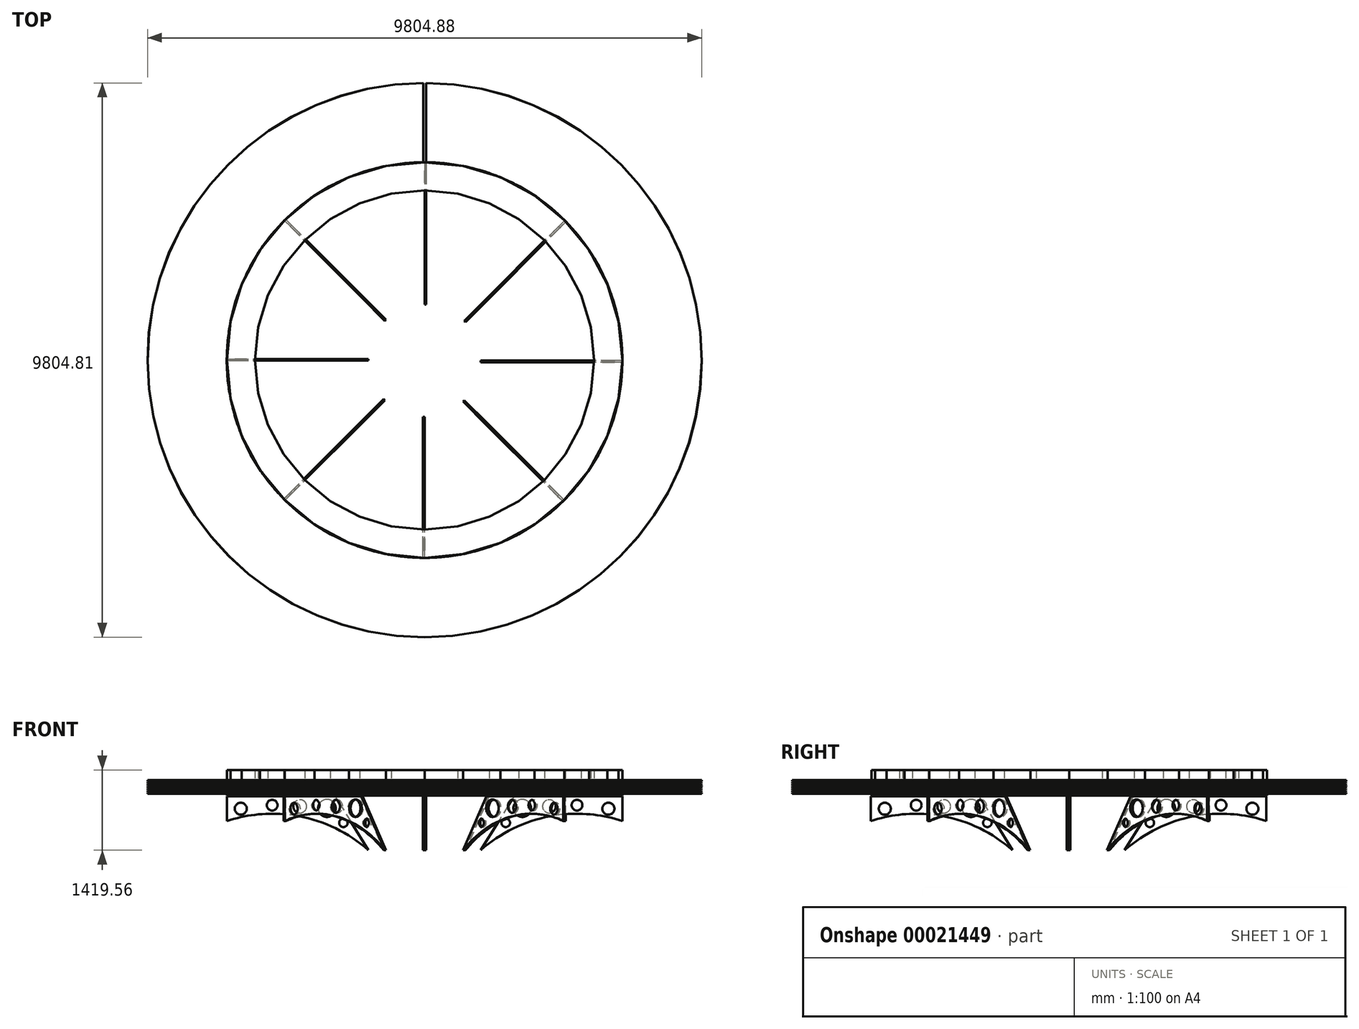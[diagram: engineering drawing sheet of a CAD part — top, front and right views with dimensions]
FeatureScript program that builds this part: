
annotation { "Feature Type Name" : "Feature", "Feature Type Description" : "" }
export const myFeature = defineFeature(function(context is Context, id is Id, definition is map)
    precondition{}
    {
        {
            var Q0;
            Q0=qCreatedBy(makeId("Right.planeOp"),FACE);
            var sketch = newSketch(context, id + "F0", { "sketchPlane" : qUnion([Q0])});
            skLineSegment(sketch, "E0", {"start": v(0, -239.01) * mm, "end": v(0, 243.44) * mm, "construction": true});
            skLineSegment(sketch, "E1", {"start": v(3500, 46.8) * mm, "end": v(3500, -314.16) * mm, "construction": true});
            skLineSegment(sketch, "E2.bottom", {"start": v(3502.44, -51) * mm, "end": v(4902.44, -51) * mm});
            skLineSegment(sketch, "E2.top", {"start": v(3502.44, -70.04) * mm, "end": v(4902.44, -70.04) * mm});
            skLineSegment(sketch, "E2.left", {"start": v(3502.44, -51) * mm, "end": v(3502.44, -70.04) * mm});
            skLineSegment(sketch, "E2.right", {"start": v(4902.44, -51) * mm, "end": v(4902.44, -70.04) * mm});
            skLineSegment(sketch, "E3.bottom", {"start": v(3501.2, 44.95) * mm, "end": v(4901.2, 44.95) * mm});
            skLineSegment(sketch, "E3.top", {"start": v(3501.2, 25.9) * mm, "end": v(4901.2, 25.9) * mm});
            skLineSegment(sketch, "E3.left", {"start": v(3501.2, 44.95) * mm, "end": v(3501.2, 25.9) * mm});
            skLineSegment(sketch, "E3.right", {"start": v(4901.2, 44.95) * mm, "end": v(4901.2, 25.9) * mm});
            skLineSegment(sketch, "E4.bottom", {"start": v(3500.35, 11.59) * mm, "end": v(4900.35, 11.59) * mm});
            skLineSegment(sketch, "E4.top", {"start": v(3500.35, -7.46) * mm, "end": v(4900.35, -7.46) * mm});
            skLineSegment(sketch, "E4.left", {"start": v(3500.35, 11.59) * mm, "end": v(3500.35, -7.46) * mm});
            skLineSegment(sketch, "E4.right", {"start": v(4900.35, 11.59) * mm, "end": v(4900.35, -7.46) * mm});
            skLineSegment(sketch, "E5.bottom", {"start": v(3500.35, -19.24) * mm, "end": v(4900.35, -19.24) * mm});
            skLineSegment(sketch, "E5.top", {"start": v(3500.35, -38.3) * mm, "end": v(4900.35, -38.3) * mm});
            skLineSegment(sketch, "E5.left", {"start": v(3500.35, -19.24) * mm, "end": v(3500.35, -38.3) * mm});
            skLineSegment(sketch, "E5.right", {"start": v(4900.35, -19.24) * mm, "end": v(4900.35, -38.3) * mm});
            skLineSegment(sketch, "E6.bottom", {"start": v(3500.35, -82.57) * mm, "end": v(4900.35, -82.57) * mm});
            skLineSegment(sketch, "E6.top", {"start": v(3500.35, -101.62) * mm, "end": v(4900.35, -101.62) * mm});
            skLineSegment(sketch, "E6.left", {"start": v(3500.35, -82.57) * mm, "end": v(3500.35, -101.62) * mm});
            skLineSegment(sketch, "E6.right", {"start": v(4900.35, -82.57) * mm, "end": v(4900.35, -101.62) * mm});
            skLineSegment(sketch, "E7.bottom", {"start": v(3500.32, -114.32) * mm, "end": v(4900.32, -114.32) * mm});
            skLineSegment(sketch, "E7.top", {"start": v(3500.32, -133.37) * mm, "end": v(4900.32, -133.37) * mm});
            skLineSegment(sketch, "E7.left", {"start": v(3500.32, -114.32) * mm, "end": v(3500.32, -133.37) * mm});
            skLineSegment(sketch, "E7.right", {"start": v(4900.32, -114.32) * mm, "end": v(4900.32, -133.37) * mm});
            skLineSegment(sketch, "E8.bottom", {"start": v(3499.61, -146.07) * mm, "end": v(4899.61, -146.07) * mm});
            skLineSegment(sketch, "E8.top", {"start": v(3499.61, -165.12) * mm, "end": v(4899.61, -165.12) * mm});
            skLineSegment(sketch, "E8.left", {"start": v(3499.61, -146.07) * mm, "end": v(3499.61, -165.12) * mm});
            skLineSegment(sketch, "E8.right", {"start": v(4899.61, -146.07) * mm, "end": v(4899.61, -165.12) * mm});
            skLineSegment(sketch, "E9.bottom", {"start": v(3501.02, -177.82) * mm, "end": v(4901.02, -177.82) * mm});
            skLineSegment(sketch, "E9.top", {"start": v(3501.02, -196.87) * mm, "end": v(4901.02, -196.87) * mm});
            skLineSegment(sketch, "E9.left", {"start": v(3501.02, -177.82) * mm, "end": v(3501.02, -196.87) * mm});
            skLineSegment(sketch, "E9.right", {"start": v(4901.02, -177.82) * mm, "end": v(4901.02, -196.87) * mm});
            skSolve(sketch);
        }
        {
            var Q0;
            Q0 = qSketchRegion(id + "F0", true);
            var Q1;
            Q1=makeQuery(id+"F0.imprint","IMPRINT",FACE,{"disambiguationData":[TD([[makeQuery(id+"F0.imprint","IMPRINT",EDGE,{"derivedFrom":sQuery(id+"F0.wireOp",EDGE,"a184cd75-155f-43dc-a134-a5bacd294978.bottom")}),-1.0]])]});
            var Q2;
            Q2=makeQuery(id+"F0.imprint","IMPRINT",FACE,{"disambiguationData":[TD([[makeQuery(id+"F0.imprint","IMPRINT",EDGE,{"derivedFrom":sQuery(id+"F0.wireOp",EDGE,"fjByr01p-CYJO-xpDp-eN8X-1QEVHWdnVLIz.bottom")}),-1.0]])]});
            var Q3;
            Q3=sQuery(id+"F0.wireOp",EDGE,"E0");
            revolve(context, id + "F1", {"entities" : qUnion([Q0, Q1, Q2]), "axis" : qUnion([Q3]), "revolveType" : RevolveType.FULL, "oppositeDirection" : true});
        }
        {
            var Q0;
            Q0=qCreatedBy(makeId("Right.planeOp"),FACE);
            var sketch = newSketch(context, id + "F2", { "sketchPlane" : qUnion([Q0])});
            skLineSegment(sketch, "E10", {"start": v(-9.7, -1234.4) * mm, "end": v(990.3, -1234.4) * mm});
            skArc(sketch, "E11", {"start": v(3490.3, -869.99) * mm, "mid": v(4263.6, -710.65) * mm, "end": v(4945.83, -313.21) * mm});
            skLineSegment(sketch, "E12", {"start": v(4990.3, -228.8) * mm, "end": v(4990.3, 71.2) * mm});
            skArc(sketch, "E13", {"start": v(4990.3, 71.2) * mm, "mid": v(4981.38, 107.51) * mm, "end": v(4956.68, 135.57) * mm});
            skArc(sketch, "E14", {"start": v(4956.68, 135.57) * mm, "mid": v(4283.38, 617.2) * mm, "end": v(3490.3, 854.45) * mm});
            skLineSegment(sketch, "E15", {"start": v(3219.3, 1091.7) * mm, "end": v(3037.04, 1091.7) * mm});
            skLineSegment(sketch, "E16", {"start": v(3037.04, 1091.7) * mm, "end": v(3037.04, 953.8) * mm});
            skLineSegment(sketch, "E17", {"start": v(3037.04, 953.8) * mm, "end": v(1578.54, 953.8) * mm});
            skLineSegment(sketch, "E18", {"start": v(-9.7, 1924.92) * mm, "end": v(-9.7, -1792.63) * mm, "construction": true});
            skLineSegment(sketch, "E19", {"start": v(1587.03, 148.03) * mm, "end": v(-9.7, 148.03) * mm});
            skArc(sketch, "E20", {"start": v(3490.3, 854.45) * mm, "mid": v(3405.26, 1030.7) * mm, "end": v(3219.3, 1091.7) * mm});
            skArc(sketch, "E21", {"start": v(4945.83, -313.21) * mm, "mid": v(4978.5, -276.5) * mm, "end": v(4990.3, -228.8) * mm});
            skLineSegment(sketch, "E22", {"start": v(1587.03, 148.03) * mm, "end": v(1578.54, 953.8) * mm});
            skArc(sketch, "E23", {"start": v(3490.3, -699.67) * mm, "mid": v(2166.77, -623.3) * mm, "end": v(990.3, -1234.4) * mm});
            skLineSegment(sketch, "E24", {"start": v(3490.3, -869.99) * mm, "end": v(3490.3, -699.67) * mm});
            skArc(sketch, "E25", {"start": v(1578.54, 953.8) * mm, "mid": v(949.34, 1709.1) * mm, "end": v(-9.7, 1924.92) * mm});
            skSolve(sketch);
        }
        {
            var Q0;
            Q0=sQuery(id+"F2.wireOp",EDGE,"E10");
            var Q1;
            Q1=sQuery(id+"F2.wireOp",EDGE,"E11");
            var Q2;
            Q2=sQuery(id+"F2.wireOp",EDGE,"E12");
            var Q3;
            Q3=sQuery(id+"F2.wireOp",EDGE,"E13");
            var Q4;
            Q4=sQuery(id+"F2.wireOp",EDGE,"E14");
            var Q5;
            Q5=sQuery(id+"F2.wireOp",EDGE,"E15");
            var Q6;
            Q6=sQuery(id+"F2.wireOp",EDGE,"E16");
            var Q7;
            Q7=sQuery(id+"F2.wireOp",EDGE,"E17");
            var Q8;
            Q8=sQuery(id+"F2.wireOp",EDGE,"E19");
            var Q9;
            Q9=sQuery(id+"F2.wireOp",EDGE,"E20");
            var Q10;
            Q10=sQuery(id+"F2.wireOp",EDGE,"E21");
            var Q11;
            Q11=sQuery(id+"F2.wireOp",EDGE,"E22");
            var Q12;
            Q12=sQuery(id+"F2.wireOp",EDGE,"E23");
            var Q13;
            Q13=sQuery(id+"F2.wireOp",EDGE,"E24");
            var Q14;
            Q14=sQuery(id+"F2.wireOp",EDGE,"E18");
            revolve(context, id + "F3", {"bodyType" : ToolBodyType.SURFACE, "surfaceEntities" : qUnion([Q0, Q1, Q2, Q3, Q4, Q5, Q6, Q7, Q8, Q9, Q10, Q11, Q12, Q13]), "axis" : qUnion([Q14]), "revolveType" : RevolveType.FULL});
        }
        {
            var Q0;
            Q0=makeQuery(id+"F1.opRevolve","SWEPT_FACE",FACE,{"disambiguationData":[OSD([sQuery(id+"F0.wireOp",EDGE,"E3.bottom")])]});
            var sketch = newSketch(context, id + "F4", { "sketchPlane" : qUnion([Q0])});
            skLineSegment(sketch, "E26.top", {"start": v(-25, 2844.2) * mm, "end": v(25, 2844.2) * mm});
            skLineSegment(sketch, "E26.left", {"start": v(-25, 5174.63) * mm, "end": v(-25, 2844.2) * mm});
            skLineSegment(sketch, "E26.right", {"start": v(25, 5174.63) * mm, "end": v(25, 2844.2) * mm});
            skLineSegment(sketch, "E27", {"start": v(0, 2844.2) * mm, "end": v(0, 3547.91) * mm, "construction": true});
            skLineSegment(sketch, "E28", {"start": v(-25, 5174.63) * mm, "end": v(25, 5174.63) * mm});
            skSolve(sketch);
        }
        {
            var Q0;
            Q0 = qSketchRegion(id + "F4", true);
            extrude(context, id + "F5", {"entities" : qUnion([Q0]), "operationType" : NewBodyOperationType.REMOVE, "oppositeDirection" : true, "depth" : 1000 * mm});
        }
        {
            var Q0;
            Q0=qCreatedBy(makeId("Top.planeOp"),FACE);
            var sketch = newSketch(context, id + "F6", { "sketchPlane" : qUnion([Q0])});
            skCircle(sketch, "E29.cCircle", {"center": v(0, 0) * mm, "radius": 3500 * mm, "construction": true});
            skLineSegment(sketch, "E29.0", {"start": v(3500, 0) * mm, "end": v(3432.75, -682.82) * mm});
            skLineSegment(sketch, "E29.1", {"start": v(3432.75, -682.82) * mm, "end": v(3233.58, -1339.4) * mm});
            skLineSegment(sketch, "E29.2", {"start": v(3233.58, -1339.4) * mm, "end": v(2910.14, -1944.5) * mm});
            skLineSegment(sketch, "E29.3", {"start": v(2910.14, -1944.5) * mm, "end": v(2474.87, -2474.87) * mm});
            skLineSegment(sketch, "E29.4", {"start": v(2474.87, -2474.87) * mm, "end": v(1944.5, -2910.14) * mm});
            skLineSegment(sketch, "E29.5", {"start": v(1944.5, -2910.14) * mm, "end": v(1339.4, -3233.58) * mm});
            skLineSegment(sketch, "E29.6", {"start": v(1339.4, -3233.58) * mm, "end": v(682.82, -3432.75) * mm});
            skLineSegment(sketch, "E29.7", {"start": v(682.82, -3432.75) * mm, "end": v(0, -3500) * mm});
            skLineSegment(sketch, "E29.8", {"start": v(0, -3500) * mm, "end": v(-682.82, -3432.75) * mm});
            skLineSegment(sketch, "E29.9", {"start": v(-682.82, -3432.75) * mm, "end": v(-1339.4, -3233.58) * mm});
            skLineSegment(sketch, "E29.10", {"start": v(-1339.4, -3233.58) * mm, "end": v(-1944.5, -2910.14) * mm});
            skLineSegment(sketch, "E29.11", {"start": v(-1944.5, -2910.14) * mm, "end": v(-2474.87, -2474.87) * mm});
            skLineSegment(sketch, "E29.12", {"start": v(-2474.87, -2474.87) * mm, "end": v(-2910.14, -1944.5) * mm});
            skLineSegment(sketch, "E29.13", {"start": v(-2910.14, -1944.5) * mm, "end": v(-3233.58, -1339.4) * mm});
            skLineSegment(sketch, "E29.14", {"start": v(-3233.58, -1339.4) * mm, "end": v(-3432.75, -682.82) * mm});
            skLineSegment(sketch, "E29.15", {"start": v(-3432.75, -682.82) * mm, "end": v(-3500, 0) * mm});
            skLineSegment(sketch, "E29.16", {"start": v(-3500, 0) * mm, "end": v(-3432.75, 682.82) * mm});
            skLineSegment(sketch, "E29.17", {"start": v(-3432.75, 682.82) * mm, "end": v(-3233.58, 1339.4) * mm});
            skLineSegment(sketch, "E29.18", {"start": v(-3233.58, 1339.4) * mm, "end": v(-2910.14, 1944.5) * mm});
            skLineSegment(sketch, "E29.19", {"start": v(-2910.14, 1944.5) * mm, "end": v(-2474.87, 2474.87) * mm});
            skLineSegment(sketch, "E29.20", {"start": v(-2474.87, 2474.87) * mm, "end": v(-1944.5, 2910.14) * mm});
            skLineSegment(sketch, "E29.21", {"start": v(-1944.5, 2910.14) * mm, "end": v(-1339.4, 3233.58) * mm});
            skLineSegment(sketch, "E29.22", {"start": v(-1339.4, 3233.58) * mm, "end": v(-682.82, 3432.75) * mm});
            skLineSegment(sketch, "E29.23", {"start": v(-682.82, 3432.75) * mm, "end": v(0, 3500) * mm});
            skLineSegment(sketch, "E29.24", {"start": v(0, 3500) * mm, "end": v(682.82, 3432.75) * mm});
            skLineSegment(sketch, "E29.25", {"start": v(682.82, 3432.75) * mm, "end": v(1339.4, 3233.58) * mm});
            skLineSegment(sketch, "E29.26", {"start": v(1339.4, 3233.58) * mm, "end": v(1944.5, 2910.14) * mm});
            skLineSegment(sketch, "E29.27", {"start": v(1944.5, 2910.14) * mm, "end": v(2474.87, 2474.87) * mm});
            skLineSegment(sketch, "E29.28", {"start": v(2474.87, 2474.87) * mm, "end": v(2910.14, 1944.5) * mm});
            skLineSegment(sketch, "E29.29", {"start": v(2910.14, 1944.5) * mm, "end": v(3233.58, 1339.4) * mm});
            skLineSegment(sketch, "E29.30", {"start": v(3233.58, 1339.4) * mm, "end": v(3432.75, 682.82) * mm});
            skLineSegment(sketch, "E29.31", {"start": v(3432.75, 682.82) * mm, "end": v(3500, 0) * mm});
            skCircle(sketch, "E30.cCircle", {"center": v(0, 0) * mm, "radius": 3000 * mm, "construction": true});
            skLineSegment(sketch, "E30.0", {"start": v(3000, 0) * mm, "end": v(2942.36, -585.27) * mm});
            skLineSegment(sketch, "E30.1", {"start": v(2942.36, -585.27) * mm, "end": v(2771.64, -1148.05) * mm});
            skLineSegment(sketch, "E30.2", {"start": v(2771.64, -1148.05) * mm, "end": v(2494.4, -1666.71) * mm});
            skLineSegment(sketch, "E30.3", {"start": v(2494.4, -1666.71) * mm, "end": v(2121.32, -2121.32) * mm});
            skLineSegment(sketch, "E30.4", {"start": v(2121.32, -2121.32) * mm, "end": v(1666.71, -2494.4) * mm});
            skLineSegment(sketch, "E30.5", {"start": v(1666.71, -2494.4) * mm, "end": v(1148.05, -2771.64) * mm});
            skLineSegment(sketch, "E30.6", {"start": v(1148.05, -2771.64) * mm, "end": v(585.27, -2942.36) * mm});
            skLineSegment(sketch, "E30.7", {"start": v(585.27, -2942.36) * mm, "end": v(0, -3000) * mm});
            skLineSegment(sketch, "E30.8", {"start": v(0, -3000) * mm, "end": v(-585.27, -2942.36) * mm});
            skLineSegment(sketch, "E30.9", {"start": v(-585.27, -2942.36) * mm, "end": v(-1148.05, -2771.64) * mm});
            skLineSegment(sketch, "E30.10", {"start": v(-1148.05, -2771.64) * mm, "end": v(-1666.71, -2494.4) * mm});
            skLineSegment(sketch, "E30.11", {"start": v(-1666.71, -2494.4) * mm, "end": v(-2121.32, -2121.32) * mm});
            skLineSegment(sketch, "E30.12", {"start": v(-2121.32, -2121.32) * mm, "end": v(-2494.4, -1666.71) * mm});
            skLineSegment(sketch, "E30.13", {"start": v(-2494.4, -1666.71) * mm, "end": v(-2771.64, -1148.05) * mm});
            skLineSegment(sketch, "E30.14", {"start": v(-2771.64, -1148.05) * mm, "end": v(-2942.36, -585.27) * mm});
            skLineSegment(sketch, "E30.15", {"start": v(-2942.36, -585.27) * mm, "end": v(-3000, 0) * mm});
            skLineSegment(sketch, "E30.16", {"start": v(-3000, 0) * mm, "end": v(-2942.36, 585.27) * mm});
            skLineSegment(sketch, "E30.17", {"start": v(-2942.36, 585.27) * mm, "end": v(-2771.64, 1148.05) * mm});
            skLineSegment(sketch, "E30.18", {"start": v(-2771.64, 1148.05) * mm, "end": v(-2494.4, 1666.71) * mm});
            skLineSegment(sketch, "E30.19", {"start": v(-2494.4, 1666.71) * mm, "end": v(-2121.32, 2121.32) * mm});
            skLineSegment(sketch, "E30.20", {"start": v(-2121.32, 2121.32) * mm, "end": v(-1666.71, 2494.4) * mm});
            skLineSegment(sketch, "E30.21", {"start": v(-1666.71, 2494.4) * mm, "end": v(-1148.05, 2771.64) * mm});
            skLineSegment(sketch, "E30.22", {"start": v(-1148.05, 2771.64) * mm, "end": v(-585.27, 2942.36) * mm});
            skLineSegment(sketch, "E30.23", {"start": v(-585.27, 2942.36) * mm, "end": v(0, 3000) * mm});
            skLineSegment(sketch, "E30.24", {"start": v(0, 3000) * mm, "end": v(585.27, 2942.36) * mm});
            skLineSegment(sketch, "E30.25", {"start": v(585.27, 2942.36) * mm, "end": v(1148.05, 2771.64) * mm});
            skLineSegment(sketch, "E30.26", {"start": v(1148.05, 2771.64) * mm, "end": v(1666.71, 2494.4) * mm});
            skLineSegment(sketch, "E30.27", {"start": v(1666.71, 2494.4) * mm, "end": v(2121.32, 2121.32) * mm});
            skLineSegment(sketch, "E30.28", {"start": v(2121.32, 2121.32) * mm, "end": v(2494.4, 1666.71) * mm});
            skLineSegment(sketch, "E30.29", {"start": v(2494.4, 1666.71) * mm, "end": v(2771.64, 1148.05) * mm});
            skLineSegment(sketch, "E30.30", {"start": v(2771.64, 1148.05) * mm, "end": v(2942.36, 585.27) * mm});
            skLineSegment(sketch, "E30.31", {"start": v(2942.36, 585.27) * mm, "end": v(3000, 0) * mm});
            skSolve(sketch);
        }
        {
            var Q0;
            Q0=makeQuery(id+"F6.imprint","IMPRINT",FACE,{"disambiguationData":[TD([[makeQuery(id+"F6.imprint","IMPRINT",EDGE,{"derivedFrom":sQuery(id+"F6.wireOp",EDGE,"E29.0")}),-1.0]])]});
            extrude(context, id + "F7", {"entities" : qUnion([Q0]), "operationType" : NewBodyOperationType.ADD, "depth" : 450 * mm, "symmetric" : true});
        }
        {
            var Q0;
            Q0=sQuery(id+"F2.wireOp",EDGE,"E25");
            var Q1;
            Q1=sQuery(id+"F2.wireOp",EDGE,"E18");
            revolve(context, id + "F8", {"bodyType" : ToolBodyType.SURFACE, "operationType" : NewBodyOperationType.ADD, "surfaceEntities" : qUnion([Q0]), "axis" : qUnion([Q1]), "revolveType" : RevolveType.FULL});
        }
        {
            var Q0;
            Q0=qCreatedBy(makeId("Right.planeOp"),FACE);
            var sketch = newSketch(context, id + "F9", { "sketchPlane" : qUnion([Q0])});
            skArc(sketch, "E31", {"start": v(3488.71, -677.06) * mm, "mid": v(2166.94, -602.06) * mm, "end": v(983.03, -1194.56) * mm});
            skLineSegment(sketch, "E32", {"start": v(3488.71, -677.06) * mm, "end": v(3488.71, -242.28) * mm});
            skLineSegment(sketch, "E33", {"start": v(3488.71, -242.28) * mm, "end": v(1571.17, -242.28) * mm});
            skLineSegment(sketch, "E34", {"start": v(1571.17, -242.28) * mm, "end": v(983.03, -1194.56) * mm});
            skCircle(sketch, "E35", {"center": v(1718.22, -450.46) * mm, "radius": 155.68 * mm});
            skCircle(sketch, "E36", {"center": v(3242.66, -459.67) * mm, "radius": 106.71 * mm});
            skPoint(sketch, "E36.centerSnap0", {"position": v(3488.71, -459.67) * mm});
            skCircle(sketch, "E37", {"center": v(2686.87, -397.53) * mm, "radius": 95.28 * mm});
            skCircle(sketch, "E38", {"center": v(2194.6, -418.7) * mm, "radius": 117.17 * mm});
            skCircle(sketch, "E39", {"center": v(1427.1, -709.82) * mm, "radius": 75.23 * mm});
            skSolve(sketch);
        }
        {
            var Q0;
            Q0 = qSketchRegion(id + "F9", true);
            var Q1;
            Q1=makeQuery(id+"F9.imprint","IMPRINT",FACE,{"disambiguationData":[TD([[makeQuery(id+"F9.imprint","IMPRINT",EDGE,{"derivedFrom":sQuery(id+"F9.wireOp",EDGE,"E31")}),-1.0]])]});
            extrude(context, id + "F10", {"entities" : qUnion([Q0, Q1]), "operationType" : NewBodyOperationType.ADD, "depth" : 30 * mm});
        }
        {
            var Q0;
            Q0=makeQuery(id+"F10.opExtrude","SWEPT_BODY",BODY,{"disambiguationData":[OSD([sQuery(id+"F9.wireOp",EDGE,"E31"),sQuery(id+"F9.wireOp",EDGE,"E32"),sQuery(id+"F9.wireOp",EDGE,"E33"),sQuery(id+"F9.wireOp",EDGE,"E34")])]});
            var Q1;
            Q1=sQuery(id+"F2.wireOp",EDGE,"E18");
            circularPattern(context, id + "F11", {"operationType" : NewBodyOperationType.ADD, "entities" : qUnion([Q0]), "axis" : qUnion([Q1]), "angle" : 360 * degree, "instanceCount" : 8, "equalSpace" : true});
        }
    });
